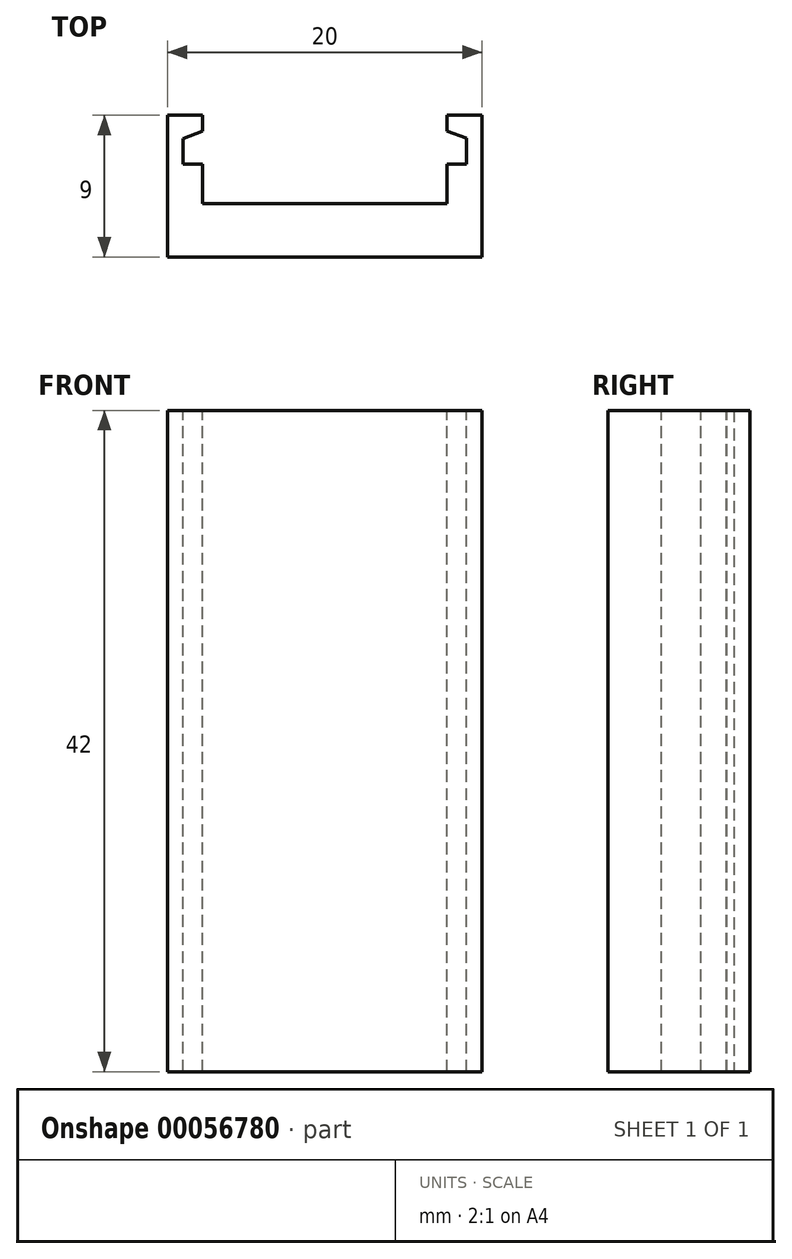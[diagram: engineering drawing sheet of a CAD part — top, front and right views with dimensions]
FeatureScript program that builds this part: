
annotation { "Feature Type Name" : "Feature", "Feature Type Description" : "" }
export const myFeature = defineFeature(function(context is Context, id is Id, definition is map)
    precondition{}
    {
        {
            var Q0;
            Q0=qCreatedBy(makeId("Front.planeOp"),FACE);
            var sketch = newSketch(context, id + "F0", { "sketchPlane" : qUnion([Q0])});
            skLineSegment(sketch, "E0.rect.bottom", {"start": v(10, 21) * mm, "end": v(-10, 21) * mm});
            skLineSegment(sketch, "E0.rect.top", {"start": v(10, -21) * mm, "end": v(-10, -21) * mm});
            skLineSegment(sketch, "E0.rect.left", {"start": v(10, 21) * mm, "end": v(10, -21) * mm});
            skLineSegment(sketch, "E0.rect.right", {"start": v(-10, 21) * mm, "end": v(-10, -21) * mm});
            skPoint(sketch, "E0.rect.middle", {"position": v(0, 0) * mm});
            skSolve(sketch);
        }
        {
            var Q0;
            Q0=makeQuery(id+"F0.imprint","IMPRINT",FACE,{"disambiguationData":[TD([[makeQuery(id+"F0.imprint","IMPRINT",EDGE,{"derivedFrom":sQuery(id+"F0.wireOp",EDGE,"E0.rect.bottom")}),1.0]])]});
            extrude(context, id + "F1", {"entities" : qUnion([Q0]), "depth" : 9 * mm});
        }
        {
            var Q0;
            Q0=makeQuery(id+"F1.opExtrude","SWEPT_FACE",FACE,{"disambiguationData":[OSD([sQuery(id+"F0.wireOp",EDGE,"E0.rect.bottom")])]});
            var sketch = newSketch(context, id + "F2", { "sketchPlane" : qUnion([Q0])});
            skLineSegment(sketch, "E1.rect.bottom", {"start": v(-7.75, 0) * mm, "end": v(7.75, 0) * mm});
            skLineSegment(sketch, "E1.rect.top", {"start": v(-7.75, -5.6) * mm, "end": v(7.75, -5.6) * mm});
            skLineSegment(sketch, "E1.rect.left", {"start": v(-7.75, 0) * mm, "end": v(-7.75, -5.6) * mm});
            skLineSegment(sketch, "E1.rect.right", {"start": v(7.75, 0) * mm, "end": v(7.75, -5.6) * mm});
            skPoint(sketch, "E1.rect.middle", {"position": v(0, 0) * mm});
            skLineSegment(sketch, "E2.bottom", {"start": v(-9, -1.5) * mm, "end": v(9, -1.5) * mm});
            skLineSegment(sketch, "E2.top", {"start": v(-9, -3.1) * mm, "end": v(9, -3.1) * mm});
            skLineSegment(sketch, "E2.left", {"start": v(-9, -1.5) * mm, "end": v(-9, -3.1) * mm});
            skLineSegment(sketch, "E2.right", {"start": v(9, -1.5) * mm, "end": v(9, -3.1) * mm});
            skSolve(sketch);
        }
        {
            var Q0;
            Q0 = qSketchRegion(id + "F2", true);
            extrude(context, id + "F3", {"entities" : qUnion([Q0]), "operationType" : NewBodyOperationType.REMOVE, "endBound" : BoundingType.THROUGH_ALL, "oppositeDirection" : true, "depth" : 25 * mm});
        }
        {
            var Q0;
            Q0=makeQuery(id+"F3.boolean.opBoolean","COPY",EDGE,{"derivedFrom":makeQuery(id+"F3.opExtrude","SWEPT_EDGE",EDGE,{"disambiguationData":[OSD([sQuery(id+"F2.wireOp",EDGE,"E1.rect.left"),sQuery(id+"F2.wireOp",EDGE,"E2.bottom")])]})});
            chamfer(context, id + "F4", {"entities" : qUnion([Q0]), "chamferType" : ChamferType.TWO_OFFSETS, "width1" : 1.3 * mm, "oppositeDirection" : false, "width2" : 0.5 * mm});
        }
        {
            var Q0;
            Q0=makeQuery(id+"F3.boolean.opBoolean","COPY",EDGE,{"derivedFrom":makeQuery(id+"F3.opExtrude","SWEPT_EDGE",EDGE,{"disambiguationData":[OSD([sQuery(id+"F2.wireOp",EDGE,"E1.rect.right"),sQuery(id+"F2.wireOp",EDGE,"E2.bottom")])]})});
            chamfer(context, id + "F5", {"entities" : qUnion([Q0]), "chamferType" : ChamferType.TWO_OFFSETS, "width1" : 1.4 * mm, "oppositeDirection" : true, "width2" : 0.5 * mm});
        }
    });
